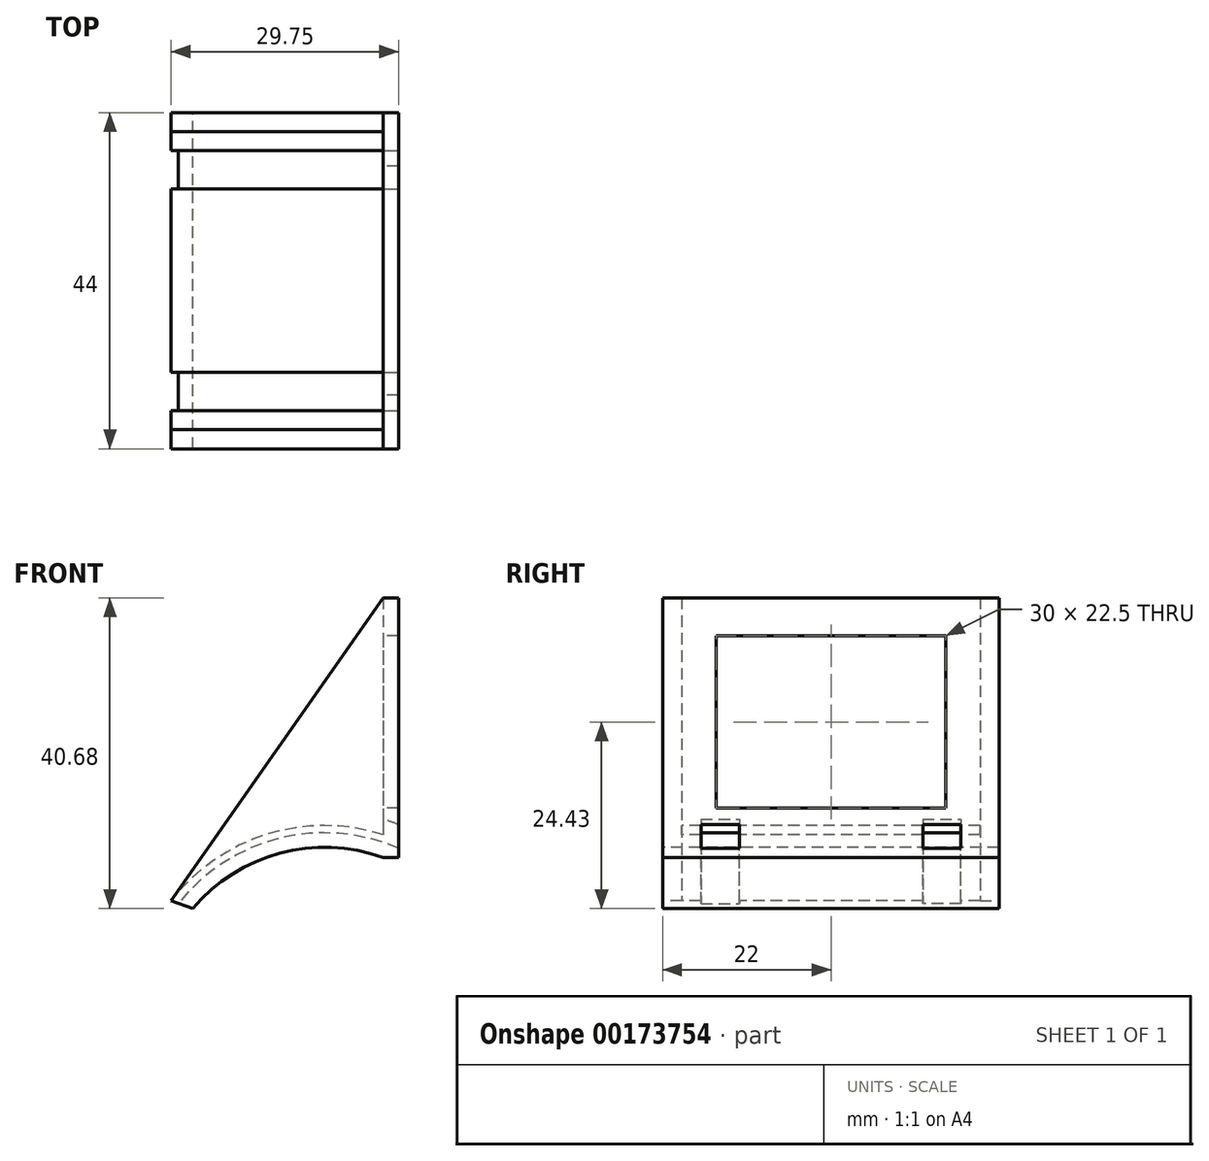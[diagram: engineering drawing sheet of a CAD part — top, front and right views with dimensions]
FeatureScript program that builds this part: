
annotation { "Feature Type Name" : "Feature", "Feature Type Description" : "" }
export const myFeature = defineFeature(function(context is Context, id is Id, definition is map)
    precondition{}
    {
        {
            var Q0;
            Q0=qCreatedBy(makeId("Right.planeOp"),FACE);
            var sketch = newSketch(context, id + "F0", { "sketchPlane" : qUnion([Q0])});
            skLineSegment(sketch, "E0.bottom", {"start": v(-22, 17) * mm, "end": v(22, 17) * mm});
            skLineSegment(sketch, "E0.top", {"start": v(-22, -17) * mm, "end": v(22, -17) * mm});
            skLineSegment(sketch, "E0.left", {"start": v(-22, 17) * mm, "end": v(-22, -17) * mm});
            skLineSegment(sketch, "E0.right", {"start": v(22, 17) * mm, "end": v(22, -17) * mm});
            skPoint(sketch, "E0.middle", {"position": v(0, 0) * mm});
            skLineSegment(sketch, "E1.bottom", {"start": v(-15, 12) * mm, "end": v(15, 12) * mm});
            skLineSegment(sketch, "E1.top", {"start": v(-15, -10.5) * mm, "end": v(15, -10.5) * mm});
            skLineSegment(sketch, "E1.left", {"start": v(-15, 12) * mm, "end": v(-15, -10.5) * mm});
            skLineSegment(sketch, "E1.right", {"start": v(15, 12) * mm, "end": v(15, -10.5) * mm});
            skSolve(sketch);
        }
        {
            var Q0;
            Q0=makeQuery(id+"F0.imprint","IMPRINT",FACE,{"disambiguationData":[TD([[makeQuery(id+"F0.imprint","IMPRINT",EDGE,{"derivedFrom":sQuery(id+"F0.wireOp",EDGE,"E0.bottom")}),-1.0]])]});
            extrude(context, id + "F1", {"entities" : qUnion([Q0]), "depth" : 2 * mm});
        }
        {
            var Q0;
            Q0=makeQuery(id+"F1.opExtrude","SWEPT_FACE",FACE,{"disambiguationData":[OSD([sQuery(id+"F0.wireOp",EDGE,"E0.left")])]});
            var sketch = newSketch(context, id + "F2", { "sketchPlane" : qUnion([Q0])});
            skLineSegment(sketch, "E2.0", {"start": v(2, -17) * mm, "end": v(0, -17) * mm, "construction": true});
            skLineSegment(sketch, "E3", {"start": v(0, -17) * mm, "end": v(10.12, -20.68) * mm, "construction": true});
            skArc(sketch, "E4", {"start": v(0, -17) * mm, "mid": v(-13.52, -16.4) * mm, "end": v(-24.93, -23.68) * mm});
            skLineSegment(sketch, "E5", {"start": v(-7.7, -38.14) * mm, "end": v(0, -17) * mm, "construction": true});
            skLineSegment(sketch, "E6", {"start": v(-7.7, -38.14) * mm, "end": v(-24.93, -23.68) * mm, "construction": true});
            skArc(sketch, "E7", {"start": v(-24.93, -23.68) * mm, "mid": v(-10.82, -15.86) * mm, "end": v(4.9, -19.5) * mm});
            skSolve(sketch);
        }
        {
            var Q0;
            Q0=makeQuery(id+"F1.opExtrude","CAP_FACE",FACE,{"disambiguationData":[OSD([sQuery(id+"F0.wireOp",EDGE,"E0.bottom"),sQuery(id+"F0.wireOp",EDGE,"E0.top"),sQuery(id+"F0.wireOp",EDGE,"E0.left"),sQuery(id+"F0.wireOp",EDGE,"E0.right"),sQuery(id+"F0.wireOp",EDGE,"E1.bottom"),sQuery(id+"F0.wireOp",EDGE,"E1.top"),sQuery(id+"F0.wireOp",EDGE,"E1.left"),sQuery(id+"F0.wireOp",EDGE,"E1.right")])],"isStart":true});
            var sketch = newSketch(context, id + "F3", { "sketchPlane" : qUnion([Q0])});
            skLineSegment(sketch, "E8.0", {"start": v(22, -17) * mm, "end": v(-22, -17) * mm});
            skLineSegment(sketch, "E9", {"start": v(-22, -17) * mm, "end": v(-22, -14) * mm});
            skLineSegment(sketch, "E10", {"start": v(-22, -14) * mm, "end": v(22, -14) * mm});
            skLineSegment(sketch, "E11", {"start": v(22, -14) * mm, "end": v(22, -17) * mm});
            skSolve(sketch);
        }
        {
            var Q0;
            Q0=makeQuery(id+"F3.imprint","IMPRINT",FACE,{"disambiguationData":[TD([[makeQuery(id+"F3.imprint","IMPRINT",EDGE,{"derivedFrom":sQuery(id+"F3.wireOp",EDGE,"E8.0")}),-1.0]])]});
            var Q1;
            Q1=sQuery(id+"F2.wireOp",EDGE,"E4");
            sweep(context, id + "F4", {"operationType" : NewBodyOperationType.ADD, "profiles" : qUnion([Q0]), "path" : qUnion([Q1])});
        }
        {
            var Q0;
            Q0=makeQuery(id+"F4.boolean.opBoolean","MERGE",FACE,{"derivedFrom":[makeQuery(id+"F1.opExtrude","SWEPT_FACE",FACE,{"disambiguationData":[OSD([sQuery(id+"F0.wireOp",EDGE,"E0.left")])]}),makeQuery(id+"F4.opSweep","SWEPT_FACE",FACE,{"disambiguationData":[OSD([sQuery(id+"F2.wireOp",EDGE,"E4"),sQuery(id+"F3.wireOp",EDGE,"E11")])]})]});
            var sketch = newSketch(context, id + "F5", { "sketchPlane" : qUnion([Q0])});
            skLineSegment(sketch, "E12", {"start": v(0, 17) * mm, "end": v(-27.75, -22.65) * mm});
            skSolve(sketch);
        }
        {
            var Q0;
            Q0=makeQuery(id+"F5.imprint","IMPRINT",FACE,{"disambiguationData":[TD([[makeQuery(id+"F5.imprint","IMPRINT",EDGE,{"derivedFrom":sQuery(id+"F5.wireOp",EDGE,"E12")}),1.0]])]});
            extrude(context, id + "F6", {"entities" : qUnion([Q0]), "operationType" : NewBodyOperationType.ADD, "oppositeDirection" : true, "depth" : 2.5 * mm});
        }
        {
            var Q0;
            Q0=makeQuery(id+"F1.opExtrude","SWEPT_BODY",BODY,{"disambiguationData":[OSD([sQuery(id+"F0.wireOp",EDGE,"E0.bottom"),sQuery(id+"F0.wireOp",EDGE,"E0.top"),sQuery(id+"F0.wireOp",EDGE,"E0.left"),sQuery(id+"F0.wireOp",EDGE,"E0.right"),sQuery(id+"F0.wireOp",EDGE,"E1.bottom"),sQuery(id+"F0.wireOp",EDGE,"E1.top"),sQuery(id+"F0.wireOp",EDGE,"E1.left"),sQuery(id+"F0.wireOp",EDGE,"E1.right")])]});
            var Q1;
            Q1=qCreatedBy(makeId("Front.planeOp"),FACE);
            mirror(context, id + "F7", {"entities" : qUnion([Q0]), "mirrorPlane" : qUnion([Q1])});
        }
        {
            var Q0;
            Q0=makeQuery(id+"F1.opExtrude","SWEPT_BODY",BODY,{"disambiguationData":[OSD([sQuery(id+"F0.wireOp",EDGE,"E0.bottom"),sQuery(id+"F0.wireOp",EDGE,"E0.top"),sQuery(id+"F0.wireOp",EDGE,"E0.left"),sQuery(id+"F0.wireOp",EDGE,"E0.right"),sQuery(id+"F0.wireOp",EDGE,"E1.bottom"),sQuery(id+"F0.wireOp",EDGE,"E1.top"),sQuery(id+"F0.wireOp",EDGE,"E1.left"),sQuery(id+"F0.wireOp",EDGE,"E1.right")])]});
            var Q1;
            Q1=makeQuery(id+"F7.opPattern","COPY",BODY,{"derivedFrom":makeQuery(id+"F1.opExtrude","SWEPT_BODY",BODY,{"disambiguationData":[OSD([sQuery(id+"F0.wireOp",EDGE,"E0.bottom"),sQuery(id+"F0.wireOp",EDGE,"E0.top"),sQuery(id+"F0.wireOp",EDGE,"E0.left"),sQuery(id+"F0.wireOp",EDGE,"E0.right"),sQuery(id+"F0.wireOp",EDGE,"E1.bottom"),sQuery(id+"F0.wireOp",EDGE,"E1.top"),sQuery(id+"F0.wireOp",EDGE,"E1.left"),sQuery(id+"F0.wireOp",EDGE,"E1.right")])]}),"instanceName":"1"});
            booleanBodies(context, id + "F8", {"operationType" : BooleanOperationType.UNION, "tools" : qUnion([Q0, Q1])});
        }
        {
            var Q0;
            Q0=makeQuery(id+"F4.opSweep","CAP_FACE",FACE,{"disambiguationData":[OSD([sQuery(id+"F2.wireOp",VERTEX,"E4.end"),sQuery(id+"F3.wireOp",EDGE,"E8.0"),sQuery(id+"F3.wireOp",EDGE,"E9"),sQuery(id+"F3.wireOp",EDGE,"E10"),sQuery(id+"F3.wireOp",EDGE,"E11")])],"isStart":false});
            var sketch = newSketch(context, id + "F9", { "sketchPlane" : qUnion([Q0])});
            skLineSegment(sketch, "E13.bottom", {"start": v(-20.33, -17) * mm, "end": v(-17.33, -17) * mm});
            skLineSegment(sketch, "E13.top", {"start": v(-20.33, -12) * mm, "end": v(-17.33, -12) * mm});
            skLineSegment(sketch, "E13.left", {"start": v(-20.33, -17) * mm, "end": v(-20.33, -12) * mm});
            skLineSegment(sketch, "E13.right", {"start": v(-17.33, -17) * mm, "end": v(-17.33, -12) * mm});
            skLineSegment(sketch, "E14.MirrorCS", {"start": v(-20.33, 17) * mm, "end": v(-20.33, 12) * mm});
            skLineSegment(sketch, "E15.MirrorCS", {"start": v(-20.33, 17) * mm, "end": v(-17.33, 17) * mm});
            skLineSegment(sketch, "E16.MirrorCS", {"start": v(-17.33, 17) * mm, "end": v(-17.33, 12) * mm});
            skLineSegment(sketch, "E17.MirrorCS", {"start": v(-20.33, 12) * mm, "end": v(-17.33, 12) * mm});
            skSolve(sketch);
        }
        {
            var Q0;
            Q0 = qSketchRegion(id + "F9", true);
            var Q1;
            Q1=sQuery(id+"F2.wireOp",EDGE,"E7");
            sweep(context, id + "F10", {"operationType" : NewBodyOperationType.REMOVE, "profiles" : qUnion([Q0]), "path" : qUnion([Q1])});
        }
    });
